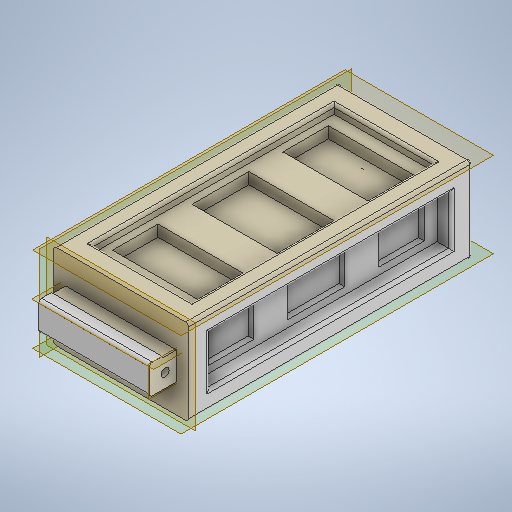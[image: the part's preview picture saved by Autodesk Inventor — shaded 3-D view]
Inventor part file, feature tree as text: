
AUTODESK INVENTOR PART (.ipt)
format: ipt  version: 2025.2 (Build 292293000, 293)  size: 968,192 bytes
history: native  units: mm
features: sketch x14, extrude x12, other x7, hole x2, fillet x2
ambient origin geometry x8: Origin, YZ Plane, XZ Plane, XY Plane, X Axis, Y Axis, Z Axis, Center Point
bodies: Body1 (feature_tree)
feature tree (37):
  other  "ソリッド1"
  extrude  "押し出し1"  Depth=47.5mm
  other  "作業平面1"
  extrude  "押し出し2"  Depth=100.0mm
  other  "作業平面2"
  hole  "穴1"  [1 undecoded]
  other  "作業平面3"
  extrude  "押し出し3"  TaperAngle=0.0deg  [1 undecoded]
  other  "作業平面4"
  extrude  "押し出し5"  Depth=39.0mm
  other  "作業平面5"
  extrude  "押し出し6"  Depth=9.76mm
  extrude  "押し出し7"  TaperAngle=0.0deg  [1 undecoded]
  extrude  "押し出し8"  TaperAngle=0.0deg  [1 undecoded]
  extrude  "押し出し9"  Depth=9.5mm TaperAngle=0.0deg
  other  "作業平面6"
  extrude  "押し出し11"  TaperAngle=0.0deg  [1 undecoded]
  extrude  "押し出し13"  Depth=4.0mm
  extrude  "押し出し14"  TaperAngle=0.0deg  [1 undecoded]
  extrude  "押し出し15"  Depth=4.5mm
  hole  "穴2"  [1 undecoded]
  fillet  "フィレット1"  [1 undecoded]
  fillet  "フィレット2"  Radius=30.0mm
  sketch  "スケッチ1"
  sketch  "スケッチ2"
  sketch  "スケッチ3"
  sketch  "スケッチ4"
  sketch  "スケッチ6"
  sketch  "スケッチ7"
  sketch  "スケッチ8"
  sketch  "スケッチ9"
  sketch  "スケッチ10"
  sketch  "スケッチ12"
  sketch  "スケッチ14"
  sketch  "スケッチ15"
  sketch  "スケッチ16"
  sketch  "スケッチ17"
note: 8 required parameter values undecoded (feature->parameter linkage not recoverable at this tier; creation-order binding heuristic only, values carry confidence <= 0.55)
